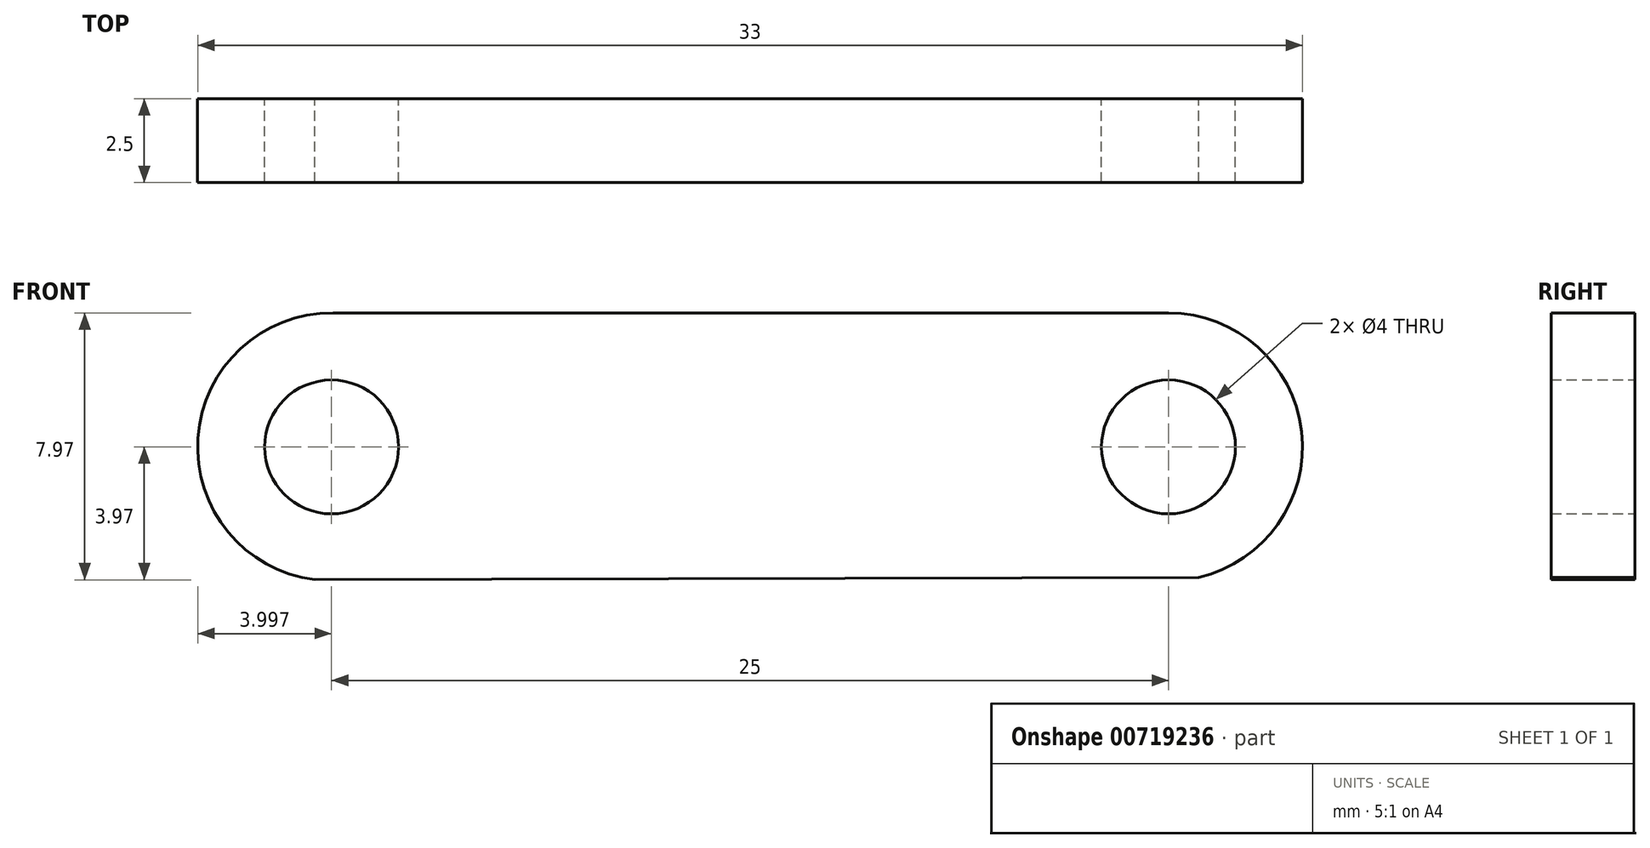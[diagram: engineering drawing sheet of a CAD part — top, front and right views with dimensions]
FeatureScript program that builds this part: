
annotation { "Feature Type Name" : "Feature", "Feature Type Description" : "" }
export const myFeature = defineFeature(function(context is Context, id is Id, definition is map)
    precondition{}
    {
        {
            var Q0;
            Q0=qCreatedBy(makeId("Front.planeOp"),FACE);
            var sketch = newSketch(context, id + "F0", { "sketchPlane" : qUnion([Q0])});
            skLineSegment(sketch, "E0", {"start": v(-12.4, 0) * mm, "end": v(12.6, 0) * mm});
            skCircle(sketch, "E1", {"center": v(-12.4, 0) * mm, "radius": 2 * mm});
            skArc(sketch, "E2", {"start": v(-12.36, 4) * mm, "mid": v(-16.4, -0.24) * mm, "end": v(-11.88, -3.97) * mm});
            skCircle(sketch, "E3", {"center": v(12.6, 0) * mm, "radius": 2 * mm});
            skArc(sketch, "E4", {"start": v(11.71, -3.9) * mm, "mid": v(16.57, -0.44) * mm, "end": v(12.6, 4) * mm});
            skLineSegment(sketch, "E5", {"start": v(-12.36, 4) * mm, "end": v(12.6, 4) * mm});
            skLineSegment(sketch, "E6", {"start": v(13.5, -3.9) * mm, "end": v(-12.9, -3.97) * mm});
            skSolve(sketch);
        }
        {
            var Q0;
            Q0=makeQuery(id+"F0.imprint","IMPRINT",FACE,{"disambiguationData":[TD([[makeQuery(id+"F0.imprint","IMPRINT",EDGE,{"derivedFrom":sQuery(id+"F0.wireOp",EDGE,"E1")}),-1.0]])]});
            extrude(context, id + "F1", {"entities" : qUnion([Q0]), "depth" : 2.5 * mm, "offsetDistance" : 25.4 * mm});
        }
    });
